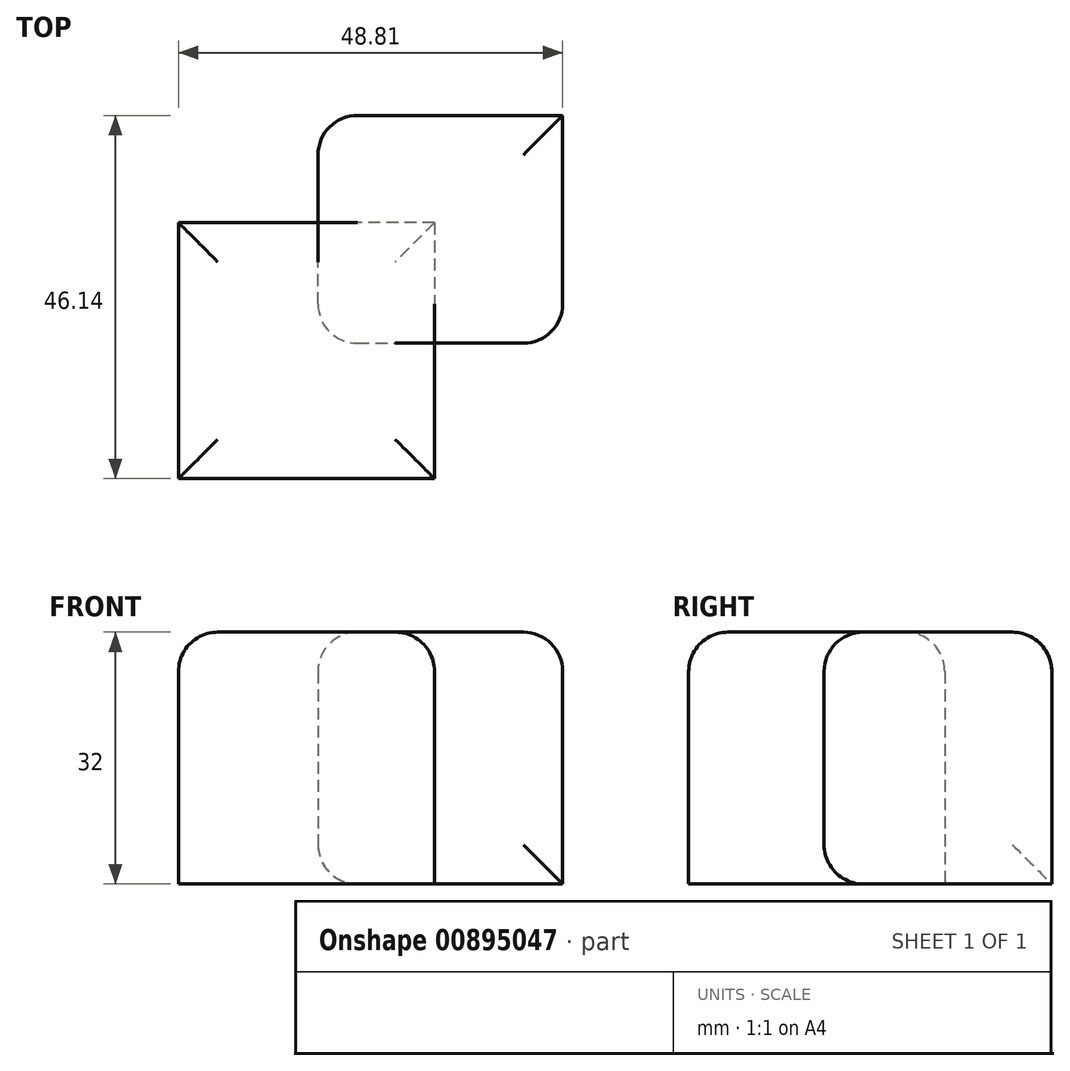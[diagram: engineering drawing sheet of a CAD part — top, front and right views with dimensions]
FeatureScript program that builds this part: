
annotation { "Feature Type Name" : "Feature", "Feature Type Description" : "" }
export const myFeature = defineFeature(function(context is Context, id is Id, definition is map)
    precondition{}
    {
        {
            var Q0;
            Q0=qCreatedBy(makeId("Top.planeOp"),FACE);
            var sketch = newSketch(context, id + "F0", { "sketchPlane" : qUnion([Q0])});
            skLineSegment(sketch, "E0.bottom", {"start": v(0, 0) * mm, "end": v(31.07, 0) * mm});
            skLineSegment(sketch, "E0.top", {"start": v(0, 28.94) * mm, "end": v(31.07, 28.94) * mm});
            skLineSegment(sketch, "E0.left", {"start": v(0, 0) * mm, "end": v(0, 28.94) * mm});
            skLineSegment(sketch, "E0.right", {"start": v(31.07, 0) * mm, "end": v(31.07, 28.94) * mm});
            skSolve(sketch);
        }
        {
            var Q0;
            Q0=qCreatedBy(makeId("Top.planeOp"),FACE);
            var sketch = newSketch(context, id + "F1", { "sketchPlane" : qUnion([Q0])});
            skLineSegment(sketch, "E1.bottom", {"start": v(14.8, 15.34) * mm, "end": v(-17.74, 15.34) * mm});
            skLineSegment(sketch, "E1.top", {"start": v(14.8, -17.2) * mm, "end": v(-17.74, -17.2) * mm});
            skLineSegment(sketch, "E1.left", {"start": v(14.8, 15.34) * mm, "end": v(14.8, -17.2) * mm});
            skLineSegment(sketch, "E1.right", {"start": v(-17.74, 15.34) * mm, "end": v(-17.74, -17.2) * mm});
            skSolve(sketch);
        }
        {
            var Q0;
            Q0=makeQuery(id+"F1.imprint","IMPRINT",FACE,{"disambiguationData":[TD([[makeQuery(id+"F1.imprint","IMPRINT",EDGE,{"derivedFrom":sQuery(id+"F1.wireOp",EDGE,"E1.bottom")}),1.0]])]});
            var Q1;
            Q1=makeQuery(id+"F0.imprint","IMPRINT",FACE,{"disambiguationData":[TD([[makeQuery(id+"F0.imprint","IMPRINT",EDGE,{"derivedFrom":sQuery(id+"F0.wireOp",EDGE,"E0.bottom")}),1.0]])]});
            extrude(context, id + "F2", {"entities" : qUnion([Q0, Q1]), "depth" : 32 * mm, "offsetDistance" : 25.4 * mm});
        }
        {
            var Q0;
            Q0=makeQuery(id+"F2.opExtrude","CAP_EDGE",EDGE,{"disambiguationData":[OSD([sQuery(id+"F0.wireOp",EDGE,"E0.top")])],"isStart":false});
            var Q1;
            Q1=makeQuery(id+"F2.opExtrude","CAP_EDGE",EDGE,{"disambiguationData":[OSD([sQuery(id+"F0.wireOp",EDGE,"E0.right")])],"isStart":false});
            fillet(context, id + "F3", {"entities" : qUnion([Q0, Q1]), "radius" : 5 * mm, "tangentPropagation" : true, "allowEdgeOverflow" : false});
        }
        {
            var Q0;
            Q0=makeQuery(id+"F2.opExtrude","SWEPT_FACE",FACE,{"disambiguationData":[OSD([sQuery(id+"F0.wireOp",EDGE,"E0.bottom")])]});
            fillet(context, id + "F4", {"entities" : qUnion([Q0]), "radius" : 5 * mm, "tangentPropagation" : true, "allowEdgeOverflow" : false});
        }
        {
            var Q0;
            Q0=makeQuery(id+"F2.opExtrude","SWEPT_FACE",FACE,{"disambiguationData":[OSD([sQuery(id+"F0.wireOp",EDGE,"E0.left")])]});
            fillet(context, id + "F5", {"entities" : qUnion([Q0]), "radius" : 5 * mm, "tangentPropagation" : true, "allowEdgeOverflow" : false});
        }
        {
            var Q0;
            Q0=makeQuery(id+"F2.opExtrude","CAP_EDGE",EDGE,{"disambiguationData":[OSD([sQuery(id+"F1.wireOp",EDGE,"E1.top")])],"isStart":false});
            var Q1;
            Q1=makeQuery(id+"F2.opExtrude","CAP_EDGE",EDGE,{"disambiguationData":[OSD([sQuery(id+"F1.wireOp",EDGE,"E1.right")])],"isStart":false});
            var Q2;
            Q2=makeQuery(id+"F2.opExtrude","CAP_EDGE",EDGE,{"disambiguationData":[OSD([sQuery(id+"F1.wireOp",EDGE,"E1.bottom")])],"isStart":false});
            var Q3;
            Q3=makeQuery(id+"F2.opExtrude","CAP_EDGE",EDGE,{"disambiguationData":[OSD([sQuery(id+"F1.wireOp",EDGE,"E1.left")])],"isStart":false});
            fillet(context, id + "F6", {"entities" : qUnion([Q0, Q1, Q2, Q3]), "radius" : 5 * mm, "tangentPropagation" : true, "allowEdgeOverflow" : false});
        }
    });
